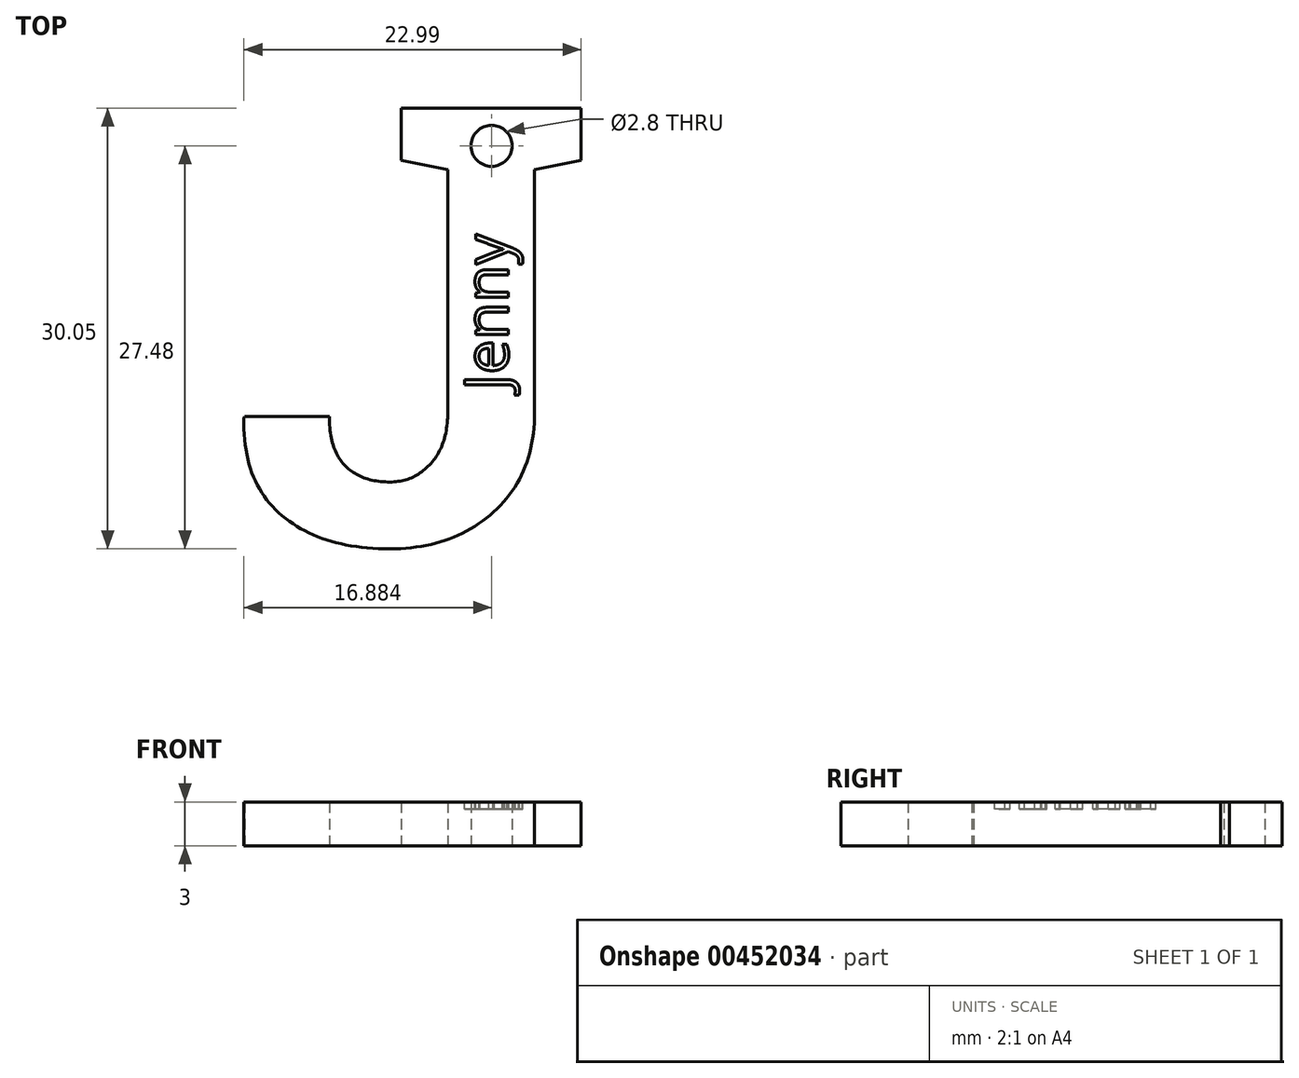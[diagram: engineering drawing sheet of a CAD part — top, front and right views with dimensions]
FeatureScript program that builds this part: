
annotation { "Feature Type Name" : "Feature", "Feature Type Description" : "" }
export const myFeature = defineFeature(function(context is Context, id is Id, definition is map)
    precondition{}
    {
        {
            var Q0;
            Q0=qCreatedBy(makeId("Top.planeOp"),FACE);
            var sketch = newSketch(context, id + "F0", { "sketchPlane" : qUnion([Q0])});
            skText(sketch, "E0", { "text": "J", "fontName": "RobotoSlab-Bold.ttf"});
            skCircle(sketch, "E1", {"center": v(17.6, 27.05) * mm, "radius": 1.4 * mm});
            const initialGuessF0  = {"E0": [0, 0, 1, 0, 0.03]};
            skSetInitialGuess(sketch, initialGuessF0);
            skSolve(sketch);
        }
        {
            var Q0;
            Q0=makeQuery(id+"F0.imprint","IMPRINT",FACE,{"disambiguationData":[TD([[makeQuery(id+"F0.imprint","IMPRINT",EDGE,{"derivedFrom":sQuery(id+"F0.wireOp",EDGE,"E0.sketch_text.stroke-0")}),-1.0]])]});
            extrude(context, id + "F1", {"entities" : qUnion([Q0]), "depth" : 3 * mm});
        }
        {
            var Q0;
            Q0=makeQuery(id+"F1.opExtrude","CAP_FACE",FACE,{"disambiguationData":[OSD([sQuery(id+"F0.wireOp",EDGE,"E0.sketch_text.stroke-0"),sQuery(id+"F0.wireOp",EDGE,"E0.sketch_text.stroke-1"),sQuery(id+"F0.wireOp",EDGE,"E0.sketch_text.stroke-2"),sQuery(id+"F0.wireOp",EDGE,"E0.sketch_text.stroke-3"),sQuery(id+"F0.wireOp",EDGE,"E0.sketch_text.stroke-4"),sQuery(id+"F0.wireOp",EDGE,"E0.sketch_text.stroke-5"),sQuery(id+"F0.wireOp",EDGE,"E0.sketch_text.stroke-6"),sQuery(id+"F0.wireOp",EDGE,"E0.sketch_text.stroke-7"),sQuery(id+"F0.wireOp",EDGE,"E0.sketch_text.stroke-8"),sQuery(id+"F0.wireOp",EDGE,"E0.sketch_text.stroke-9"),sQuery(id+"F0.wireOp",EDGE,"E0.sketch_text.stroke-10"),sQuery(id+"F0.wireOp",EDGE,"E0.sketch_text.stroke-11"),sQuery(id+"F0.wireOp",EDGE,"E0.sketch_text.stroke-12"),sQuery(id+"F0.wireOp",EDGE,"E0.sketch_text.stroke-13"),sQuery(id+"F0.wireOp",EDGE,"E0.sketch_text.stroke-14"),sQuery(id+"F0.wireOp",EDGE,"E0.sketch_text.stroke-15"),sQuery(id+"F0.wireOp",EDGE,"E0.sketch_text.stroke-16"),sQuery(id+"F0.wireOp",EDGE,"E0.sketch_text.stroke-17"),sQuery(id+"F0.wireOp",EDGE,"E1")])],"isStart":false});
            var sketch = newSketch(context, id + "F2", { "sketchPlane" : qUnion([Q0])});
            skText(sketch, "E2", { "text": "Jenny\n", "fontName": "OpenSans-Regular.ttf"});
            const initialGuessF2  = {"E2": [0.01873, 0.01037, 0, 1, 0.003]};
            skSetInitialGuess(sketch, initialGuessF2);
            skSolve(sketch);
        }
        {
            var Q0;
            Q0 = qSketchRegion(id + "F2", true);
            extrude(context, id + "F3", {"entities" : qUnion([Q0]), "operationType" : NewBodyOperationType.REMOVE, "endBound" : BoundingType.SYMMETRIC, "oppositeDirection" : true, "depth" : 1 * mm});
        }
    });
